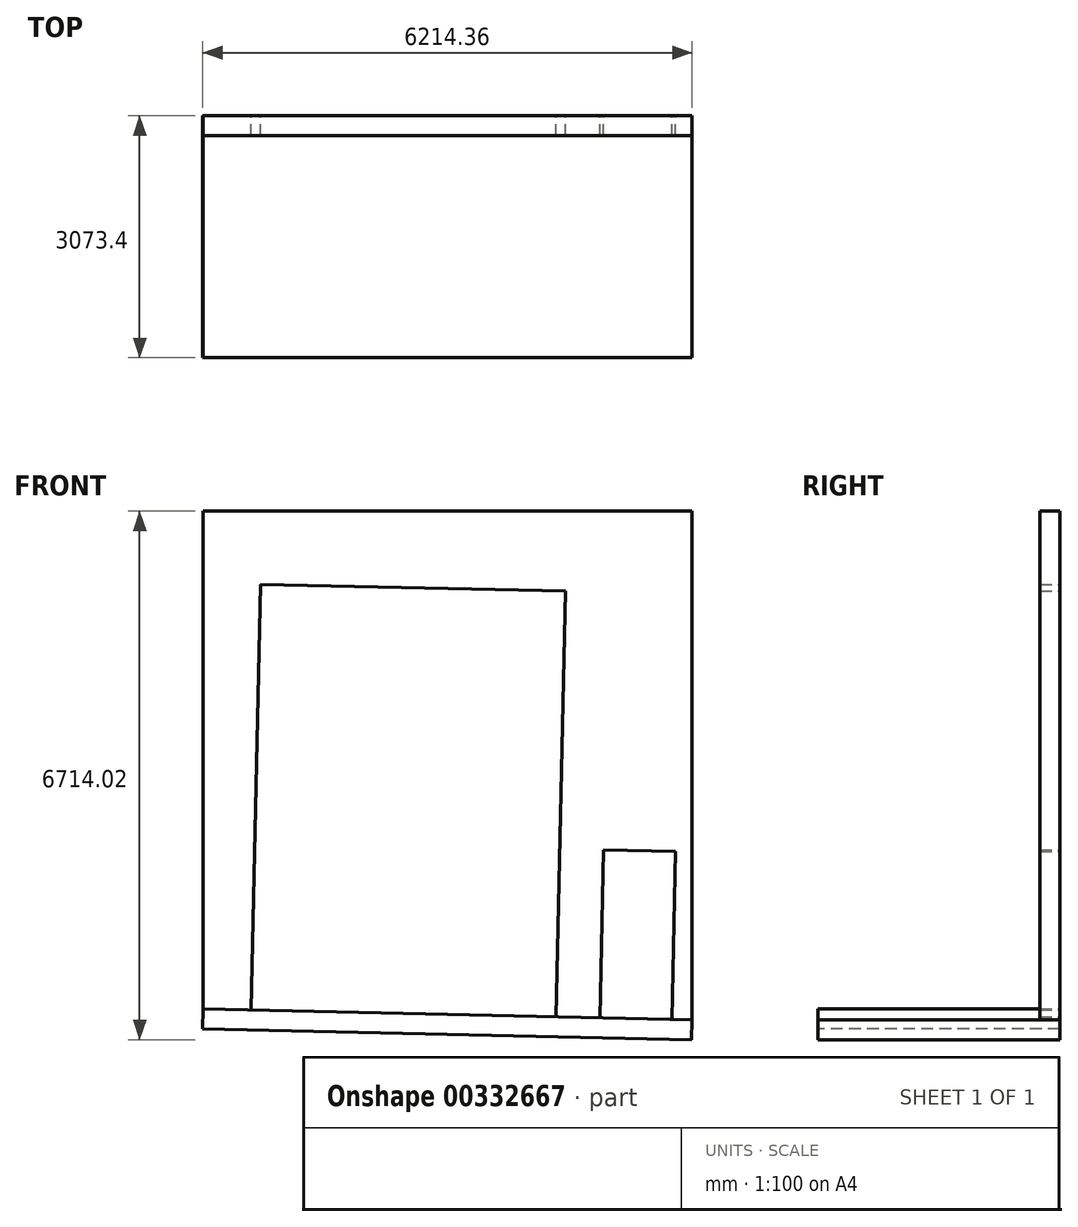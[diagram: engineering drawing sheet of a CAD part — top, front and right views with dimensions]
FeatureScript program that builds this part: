
annotation { "Feature Type Name" : "Feature", "Feature Type Description" : "" }
export const myFeature = defineFeature(function(context is Context, id is Id, definition is map)
    precondition{}
    {
        {
            var Q0;
            Q0=qCreatedBy(makeId("Front.planeOp"),FACE);
            var sketch = newSketch(context, id + "F0", { "sketchPlane" : qUnion([Q0])});
            skLineSegment(sketch, "E0", {"start": v(-5481.34, 5531.1) * mm, "end": v(-1608.77, 5446.6) * mm});
            skLineSegment(sketch, "E1", {"start": v(0, 0) * mm, "end": v(0, 6460.08) * mm});
            skLineSegment(sketch, "E2", {"start": v(0, 6460.08) * mm, "end": v(-6208.82, 6460.08) * mm});
            skLineSegment(sketch, "E3", {"start": v(-6208.82, 6460.08) * mm, "end": v(-6208.82, 135.48) * mm});
            skLineSegment(sketch, "E4", {"start": v(-6208.82, 135.48) * mm, "end": v(-5599.37, 122.18) * mm});
            skLineSegment(sketch, "E5", {"start": v(-1168.12, 25.49) * mm, "end": v(-1121.57, 2159.09) * mm});
            skLineSegment(sketch, "E6", {"start": v(-1726.79, 37.68) * mm, "end": v(-1168.12, 25.49) * mm});
            skLineSegment(sketch, "E7", {"start": v(-253.94, 5.54) * mm, "end": v(0, 0) * mm});
            skLineSegment(sketch, "E8", {"start": v(-5599.37, 122.18) * mm, "end": v(-5481.34, 5531.1) * mm});
            skLineSegment(sketch, "E9", {"start": v(-1608.77, 5446.6) * mm, "end": v(-1726.79, 37.68) * mm});
            skLineSegment(sketch, "E10", {"start": v(-207.38, 2139.14) * mm, "end": v(-253.94, 5.54) * mm});
            skLineSegment(sketch, "E11", {"start": v(-1121.57, 2159.09) * mm, "end": v(-207.38, 2139.14) * mm});
            skSolve(sketch);
        }
        {
            var Q0;
            Q0=makeQuery(id+"F0.imprint","IMPRINT",FACE,{"disambiguationData":[TD([[makeQuery(id+"F0.imprint","IMPRINT",EDGE,{"derivedFrom":sQuery(id+"F0.wireOp",EDGE,"E0")}),1.0]])]});
            extrude(context, id + "F1", {"entities" : qUnion([Q0]), "depth" : 254 * mm});
        }
        {
            var Q0;
            Q0=makeQuery(id+"F1.opExtrude","SWEPT_FACE",FACE,{"disambiguationData":[OSD([sQuery(id+"F0.wireOp",EDGE,"E4")])]});
            var sketch = newSketch(context, id + "F2", { "sketchPlane" : qUnion([Q0])});
            skLineSegment(sketch, "E12.bottom", {"start": v(-6210.3, 0) * mm, "end": v(0, 0) * mm});
            skLineSegment(sketch, "E12.top", {"start": v(-6210.3, 3073.4) * mm, "end": v(0, 3073.4) * mm});
            skLineSegment(sketch, "E12.left", {"start": v(-6210.3, 0) * mm, "end": v(-6210.3, 3073.4) * mm});
            skLineSegment(sketch, "E12.right", {"start": v(0, 0) * mm, "end": v(0, 3073.4) * mm});
            skSolve(sketch);
        }
        {
            var Q0;
            Q0 = qSketchRegion(id + "F2", true);
            extrude(context, id + "F3", {"entities" : qUnion([Q0]), "operationType" : NewBodyOperationType.ADD, "depth" : 254 * mm});
        }
    });
